# Revit family: QF_ELECTROLUXPROFESSIONAL_1L059Y_TD6-14_S
name_source: partatom
category: Attrezzature speciali
units: mm (PartAtom-declared; Revit-internal decimal feet)

## family parameters
Basato su piano di lavoro = No
Condiviso = No
Punto di calcolo locali = No
Quota connettore circolare = Usa diametro
Sempre verticale = Sì
Taglio con vuoti quando caricato = No
Tipo di parte = Normale

## types (8) — shared parameters
Height Actual = 1771 mm  [stored 5.81037 ft]
Latent Heat Output = 0.0
Length Actual = 790 mm  [stored 2.59186 ft]
Modello = TD6-14
Produttore = Electrolux Professional
Sensible Heat Output = 0.0
URL = www.electroluxprofessional.com
zero-valued in all types: Gas KW, Prospetto di default, Steam Pounds per Hour

## per-type parameters (varying)
| type | Cycle | Depth Actual | Descrizione | Item Number | Phase | Volts | Watts | Weight |
| 9873730023 | 50 Hz | 1105 mm  [stored 3.62533 ft] | TUMBLE DRYER TD6-14 14KG GALVA.DRUM STEAM 25KW 380-415/50/3N COMPASS PRO 6G81 EU SILVER DO.RIGHT MB STOP DISCON. | 1LSN2K | 3 | 415 V | 1000 W | 230 |
| 9873730109 | 50 Hz | 1105 mm  [stored 3.62533 ft] | TUMBLE DRYER TD6-14 14KG GALVA.DRUM STEAM 25KW 240/50/1N COMPASS PRO 6G82 EU SILVER DO.RIGHT STOP DISCON. | 1LSNPS | 1 | 240 V | 1200 W | 230 |
| 9873730123 | 60 Hz | 1105 mm  [stored 3.62533 ft] | TUMBLE DRYER TD6-14 14KG GALVA.DRUM STEAM 25KW 240/60/1N COMPASS PRO 6G82 EU SILVER DO.RIGHT STOP DISCON. | 1LSNV8 | 1 | 240 V | 1200 W | 230 |
| 9873730184 | 50 Hz | 965 mm  [stored 3.16601 ft] | TUMBLE DRYER TD6-14 MARINE 14KG GALVA.DRUM STEAM 25KW 400/50/3N COMPASS PRO 6G81 SE SILVER DO.RIGHT MB STOP DISCON. | 1L0H0C | 3 | 400 V | 1000 W | 222 |
| 9873730006 | 50 Hz | 1105 mm  [stored 3.62533 ft] | TUMBLE DRYER TD6-14 14KG GALVA.DRUM STEAM 25KW 380-415/50/3N COMPASS PRO 6G81 EU SILVER DO.RIGHT.INS. MB STOP DISCON. | 1L0E4S | 3 | 415 V | 1000 W | 230 |
| 9873730059 | 50 Hz | 1105 mm  [stored 3.62533 ft] | TUMBLE DRYER TD6-14 14KG SST DRUM STEAM 25KW 400/50/3 COMPASS PRO 6G81 EU SILVER DO.RIGHT MB STOP DISCON. | 1L80E3 | 3 | 400 V | 1000 W | 230 |
| 9873730122 | 60 Hz | 1105 mm  [stored 3.62533 ft] | TUMBLE DRYER TD6-14 14KG GALVA.DRUM STEAM 25KW 240/60/1N COMPASS PRO 6G81 EU SILVER DO.RIGHT MB STOP DISCON. | 1LSNV7 | 1 | 240 V | 1200 W | 230 |
| 9873730187 | 60 Hz | 965 mm  [stored 3.16601 ft] | TUMBLE DRYER TD6-14 14KG GALVA.DRUM STEAM 25KW 220/60/3 COMPASS PRO 6G82 EU SILVER DO.RIGHT STOP DISCON. EXT.CONN. | 1LSPPS | 3 | 220 V | 1000 W | 222 |

note: [stored X ft] marks values corroborated as IEEE doubles in the binary element streams (Revit-internal decimal feet)

## geometry (parser evidence)
native form markers: Blend x14
no freeform markers — native parametric forms only
